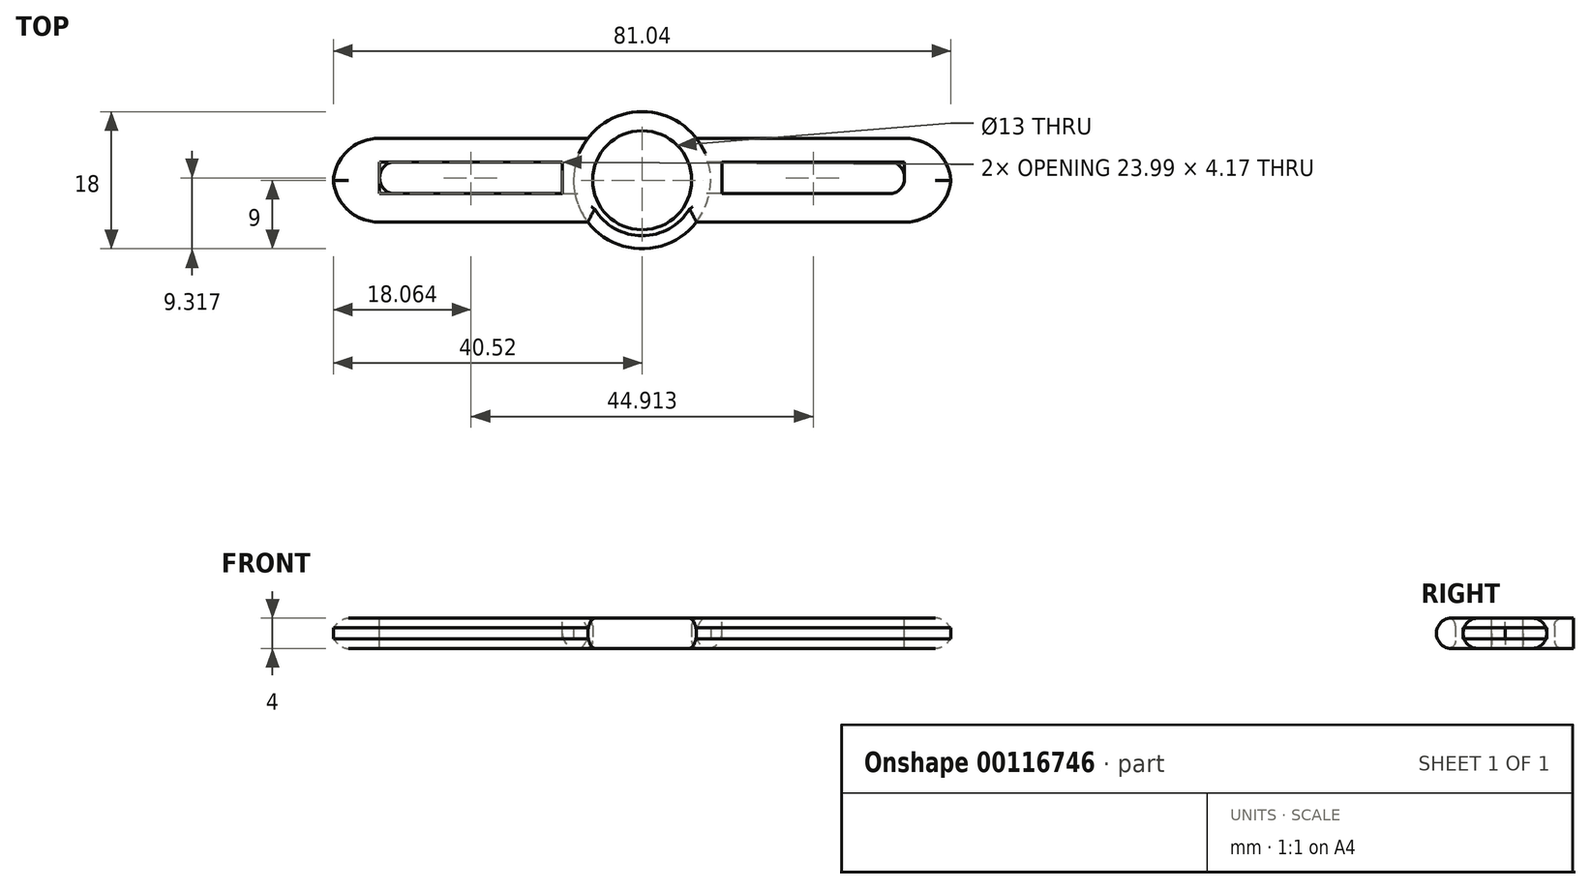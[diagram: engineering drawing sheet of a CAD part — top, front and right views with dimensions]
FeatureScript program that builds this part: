
annotation { "Feature Type Name" : "Feature", "Feature Type Description" : "" }
export const myFeature = defineFeature(function(context is Context, id is Id, definition is map)
    precondition{}
    {
        {
            var Q0;
            Q0=qCreatedBy(makeId("Top.planeOp"),FACE);
            var sketch = newSketch(context, id + "F0", { "sketchPlane" : qUnion([Q0])});
            skCircle(sketch, "E0", {"center": v(0, 0) * mm, "radius": 9 * mm});
            skCircle(sketch, "E1", {"center": v(0, 0) * mm, "radius": 6.5 * mm});
            skLineSegment(sketch, "E2.bottom", {"start": v(-40.54, -5.5) * mm, "end": v(40.54, -5.5) * mm});
            skLineSegment(sketch, "E2.top", {"start": v(-40.54, 5.5) * mm, "end": v(40.54, 5.5) * mm});
            skLineSegment(sketch, "E2.left", {"start": v(-40.54, -5.5) * mm, "end": v(-40.54, 5.5) * mm});
            skLineSegment(sketch, "E2.right", {"start": v(40.54, -5.5) * mm, "end": v(40.54, 5.5) * mm});
            skSolve(sketch);
        }
        {
            var Q0;
            {var subQ5=sQuery(id+"F0.wireOp",EDGE,"E2.left");Q0=makeQuery(id+"F0.imprint","IMPRINT",FACE,{"disambiguationData":[TD([[makeQuery(id+"F0.imprint","IMPRINT",EDGE,{"derivedFrom":subQ5}),-1.0]])]});}
            var Q1;
            {var subQ5=sQuery(id+"F0.wireOp",EDGE,"E2.right");Q1=makeQuery(id+"F0.imprint","IMPRINT",FACE,{"disambiguationData":[TD([[makeQuery(id+"F0.imprint","IMPRINT",EDGE,{"derivedFrom":subQ5}),1.0]])]});}
            extrude(context, id + "F1", {"entities" : qUnion([Q0, Q1]), "endBound" : BoundingType.SYMMETRIC, "depth" : 1.5 * mm});
        }
        {
            var Q0;
            Q0 = qSketchRegion(id + "F0", true);
            extrude(context, id + "F2", {"entities" : qUnion([Q0]), "endBound" : BoundingType.SYMMETRIC, "depth" : 4 * mm});
        }
        {
            var Q0;
            Q0=makeQuery(id+"F2.opExtrude","SWEPT_EDGE",EDGE,{"disambiguationData":[OSD([sQuery(id+"F0.wireOp",EDGE,"E2.top"),sQuery(id+"F0.wireOp",EDGE,"E2.left")])]});
            var Q1;
            Q1=makeQuery(id+"F2.opExtrude","SWEPT_EDGE",EDGE,{"disambiguationData":[OSD([sQuery(id+"F0.wireOp",EDGE,"E2.bottom"),sQuery(id+"F0.wireOp",EDGE,"E2.left")])]});
            var Q2;
            Q2=makeQuery(id+"F2.opExtrude","SWEPT_EDGE",EDGE,{"disambiguationData":[OSD([sQuery(id+"F0.wireOp",EDGE,"E2.top"),sQuery(id+"F0.wireOp",EDGE,"E2.right")])]});
            var Q3;
            Q3=makeQuery(id+"F2.opExtrude","SWEPT_EDGE",EDGE,{"disambiguationData":[OSD([sQuery(id+"F0.wireOp",EDGE,"E2.bottom"),sQuery(id+"F0.wireOp",EDGE,"E2.right")])]});
            fillet(context, id + "F3", {"entities" : qUnion([Q0, Q1, Q2, Q3]), "radius" : 6 * mm, "tangentPropagation" : true, "allowEdgeOverflow" : false});
        }
        {
            var Q0;
            Q0=makeQuery(id+"F1.opExtrude","SWEPT_EDGE",EDGE,{"disambiguationData":[OSD([sQuery(id+"F0.wireOp",EDGE,"E2.top"),sQuery(id+"F0.wireOp",EDGE,"E2.right")])]});
            var Q1;
            Q1=makeQuery(id+"F1.opExtrude","SWEPT_EDGE",EDGE,{"disambiguationData":[OSD([sQuery(id+"F0.wireOp",EDGE,"E2.bottom"),sQuery(id+"F0.wireOp",EDGE,"E2.right")])]});
            var Q2;
            Q2=makeQuery(id+"F1.opExtrude","SWEPT_EDGE",EDGE,{"disambiguationData":[OSD([sQuery(id+"F0.wireOp",EDGE,"E2.top"),sQuery(id+"F0.wireOp",EDGE,"E2.left")])]});
            var Q3;
            Q3=makeQuery(id+"F1.opExtrude","SWEPT_EDGE",EDGE,{"disambiguationData":[OSD([sQuery(id+"F0.wireOp",EDGE,"E2.bottom"),sQuery(id+"F0.wireOp",EDGE,"E2.left")])]});
            fillet(context, id + "F4", {"entities" : qUnion([Q0, Q1, Q2, Q3]), "radius" : 6 * mm, "tangentPropagation" : true, "allowEdgeOverflow" : false});
        }
        {
            var Q0;
            {var subQ0=sQuery(id+"F0.wireOp",EDGE,"E2.left");var subQ1=sQuery(id+"F0.wireOp",EDGE,"E2.bottom");Q0=makeQuery(id+"F3.opFillet","BLEND_EDGE",EDGE,{"blendedFrom":[makeQuery(id+"F2.opExtrude","SWEPT_EDGE",EDGE,{"disambiguationData":[OSD([subQ1,subQ0])]}),makeQuery(id+"F2.opExtrude","CAP_FACE",FACE,{"disambiguationData":[OSD([sQuery(id+"F0.wireOp",EDGE,"E0"),sQuery(id+"F0.wireOp",EDGE,"E1"),subQ1,sQuery(id+"F0.wireOp",EDGE,"E2.top"),subQ0,sQuery(id+"F0.wireOp",EDGE,"E2.right")])],"isStart":false})],"blendedInto":[makeQuery(id+"F2.opExtrude","CAP_FACE",FACE,{"disambiguationData":[OSD([sQuery(id+"F0.wireOp",EDGE,"E0"),sQuery(id+"F0.wireOp",EDGE,"E1"),subQ1,sQuery(id+"F0.wireOp",EDGE,"E2.top"),subQ0,sQuery(id+"F0.wireOp",EDGE,"E2.right")])],"isStart":false})]});}
            var Q1;
            {var subQ0=sQuery(id+"F0.wireOp",EDGE,"E2.left");var subQ1=sQuery(id+"F0.wireOp",EDGE,"E2.top");Q1=makeQuery(id+"F3.opFillet","BLEND_EDGE",EDGE,{"blendedFrom":[makeQuery(id+"F2.opExtrude","SWEPT_EDGE",EDGE,{"disambiguationData":[OSD([subQ1,subQ0])]}),makeQuery(id+"F2.opExtrude","CAP_FACE",FACE,{"disambiguationData":[OSD([sQuery(id+"F0.wireOp",EDGE,"E0"),sQuery(id+"F0.wireOp",EDGE,"E1"),sQuery(id+"F0.wireOp",EDGE,"E2.bottom"),subQ1,subQ0,sQuery(id+"F0.wireOp",EDGE,"E2.right")])],"isStart":false})],"blendedInto":[makeQuery(id+"F2.opExtrude","CAP_FACE",FACE,{"disambiguationData":[OSD([sQuery(id+"F0.wireOp",EDGE,"E0"),sQuery(id+"F0.wireOp",EDGE,"E1"),sQuery(id+"F0.wireOp",EDGE,"E2.bottom"),subQ1,subQ0,sQuery(id+"F0.wireOp",EDGE,"E2.right")])],"isStart":false})]});}
            var Q2;
            {var subQ0=sQuery(id+"F0.wireOp",EDGE,"E2.top");Q2=makeQuery(id+"F2.opExtrude","CAP_EDGE",EDGE,{"disambiguationData":[OSD([subQ0]),TDD([makeQuery(id+"F0.imprint","IMPRINT",EDGE,{"disambiguationData":[TD([[makeQuery(id+"F0.imprint","INTERSECT",VERTEX,{"derivedFrom":[subQ0,sQuery(id+"F0.wireOp",EDGE,"E2.left")]}),-1.0]])],"derivedFrom":subQ0})])],"isStart":false});}
            var Q3;
            {var subQ0=sQuery(id+"F0.wireOp",EDGE,"E2.bottom");Q3=makeQuery(id+"F2.opExtrude","CAP_EDGE",EDGE,{"disambiguationData":[OSD([subQ0]),TDD([makeQuery(id+"F0.imprint","IMPRINT",EDGE,{"disambiguationData":[TD([[makeQuery(id+"F0.imprint","INTERSECT",VERTEX,{"derivedFrom":[subQ0,sQuery(id+"F0.wireOp",EDGE,"E2.left")]}),-1.0]])],"derivedFrom":subQ0})])],"isStart":false});}
            var Q4;
            {var subQ0=sQuery(id+"F0.wireOp",EDGE,"E2.bottom");Q4=makeQuery(id+"F2.opExtrude","CAP_EDGE",EDGE,{"disambiguationData":[OSD([subQ0]),TDD([makeQuery(id+"F0.imprint","IMPRINT",EDGE,{"disambiguationData":[TD([[makeQuery(id+"F0.imprint","INTERSECT",VERTEX,{"derivedFrom":[subQ0,sQuery(id+"F0.wireOp",EDGE,"E2.right")]}),1.0]])],"derivedFrom":subQ0})])],"isStart":false});}
            var Q5;
            {var subQ0=sQuery(id+"F0.wireOp",EDGE,"E2.right");var subQ1=sQuery(id+"F0.wireOp",EDGE,"E2.bottom");Q5=makeQuery(id+"F3.opFillet","BLEND_EDGE",EDGE,{"blendedFrom":[makeQuery(id+"F2.opExtrude","SWEPT_EDGE",EDGE,{"disambiguationData":[OSD([subQ1,subQ0])]}),makeQuery(id+"F2.opExtrude","CAP_FACE",FACE,{"disambiguationData":[OSD([sQuery(id+"F0.wireOp",EDGE,"E0"),sQuery(id+"F0.wireOp",EDGE,"E1"),subQ1,sQuery(id+"F0.wireOp",EDGE,"E2.top"),sQuery(id+"F0.wireOp",EDGE,"E2.left"),subQ0])],"isStart":false})],"blendedInto":[makeQuery(id+"F2.opExtrude","CAP_FACE",FACE,{"disambiguationData":[OSD([sQuery(id+"F0.wireOp",EDGE,"E0"),sQuery(id+"F0.wireOp",EDGE,"E1"),subQ1,sQuery(id+"F0.wireOp",EDGE,"E2.top"),sQuery(id+"F0.wireOp",EDGE,"E2.left"),subQ0])],"isStart":false})]});}
            var Q6;
            {var subQ0=sQuery(id+"F0.wireOp",EDGE,"E2.right");var subQ1=sQuery(id+"F0.wireOp",EDGE,"E2.top");Q6=makeQuery(id+"F3.opFillet","BLEND_EDGE",EDGE,{"blendedFrom":[makeQuery(id+"F2.opExtrude","SWEPT_EDGE",EDGE,{"disambiguationData":[OSD([subQ1,subQ0])]}),makeQuery(id+"F2.opExtrude","CAP_FACE",FACE,{"disambiguationData":[OSD([sQuery(id+"F0.wireOp",EDGE,"E0"),sQuery(id+"F0.wireOp",EDGE,"E1"),sQuery(id+"F0.wireOp",EDGE,"E2.bottom"),subQ1,sQuery(id+"F0.wireOp",EDGE,"E2.left"),subQ0])],"isStart":false})],"blendedInto":[makeQuery(id+"F2.opExtrude","CAP_FACE",FACE,{"disambiguationData":[OSD([sQuery(id+"F0.wireOp",EDGE,"E0"),sQuery(id+"F0.wireOp",EDGE,"E1"),sQuery(id+"F0.wireOp",EDGE,"E2.bottom"),subQ1,sQuery(id+"F0.wireOp",EDGE,"E2.left"),subQ0])],"isStart":false})]});}
            var Q7;
            {var subQ0=sQuery(id+"F0.wireOp",EDGE,"E2.top");Q7=makeQuery(id+"F2.opExtrude","CAP_EDGE",EDGE,{"disambiguationData":[OSD([subQ0]),TDD([makeQuery(id+"F0.imprint","IMPRINT",EDGE,{"disambiguationData":[TD([[makeQuery(id+"F0.imprint","INTERSECT",VERTEX,{"derivedFrom":[subQ0,sQuery(id+"F0.wireOp",EDGE,"E2.right")]}),1.0]])],"derivedFrom":subQ0})])],"isStart":false});}
            var Q8;
            {var subQ0=sQuery(id+"F0.wireOp",EDGE,"E2.top");var subQ1=sQuery(id+"F0.wireOp",EDGE,"E0");Q8=makeQuery(id+"F2.opExtrude","CAP_EDGE",EDGE,{"disambiguationData":[OSD([subQ1]),TDD([makeQuery(id+"F0.imprint","IMPRINT",EDGE,{"disambiguationData":[TD([[makeQuery(id+"F0.imprint","INTERSECT",VERTEX,{"disambiguationData":[OD(0.0)],"derivedFrom":[subQ1,subQ0]}),1.0]])],"derivedFrom":subQ1})])],"isStart":false});}
            var Q9;
            {var subQ0=sQuery(id+"F0.wireOp",EDGE,"E2.bottom");var subQ1=sQuery(id+"F0.wireOp",EDGE,"E0");Q9=makeQuery(id+"F2.opExtrude","CAP_EDGE",EDGE,{"disambiguationData":[OSD([subQ1]),TDD([makeQuery(id+"F0.imprint","IMPRINT",EDGE,{"disambiguationData":[TD([[makeQuery(id+"F0.imprint","INTERSECT",VERTEX,{"disambiguationData":[OD(0.0)],"derivedFrom":[subQ1,subQ0]}),-1.0]])],"derivedFrom":subQ1})])],"isStart":false});}
            var Q10;
            {var subQ0=sQuery(id+"F0.wireOp",EDGE,"E2.bottom");var subQ1=sQuery(id+"F0.wireOp",EDGE,"E0");Q10=makeQuery(id+"F2.opExtrude","CAP_EDGE",EDGE,{"disambiguationData":[OSD([subQ1]),TDD([makeQuery(id+"F0.imprint","IMPRINT",EDGE,{"disambiguationData":[TD([[makeQuery(id+"F0.imprint","INTERSECT",VERTEX,{"disambiguationData":[OD(0.0)],"derivedFrom":[subQ1,subQ0]}),-1.0]])],"derivedFrom":subQ1})])],"isStart":true});}
            var Q11;
            {var subQ0=sQuery(id+"F0.wireOp",EDGE,"E2.top");var subQ1=sQuery(id+"F0.wireOp",EDGE,"E0");Q11=makeQuery(id+"F2.opExtrude","CAP_EDGE",EDGE,{"disambiguationData":[OSD([subQ1]),TDD([makeQuery(id+"F0.imprint","IMPRINT",EDGE,{"disambiguationData":[TD([[makeQuery(id+"F0.imprint","INTERSECT",VERTEX,{"disambiguationData":[OD(0.0)],"derivedFrom":[subQ1,subQ0]}),1.0]])],"derivedFrom":subQ1})])],"isStart":true});}
            var Q12;
            {var subQ0=sQuery(id+"F0.wireOp",EDGE,"E2.bottom");Q12=makeQuery(id+"F2.opExtrude","CAP_EDGE",EDGE,{"disambiguationData":[OSD([subQ0]),TDD([makeQuery(id+"F0.imprint","IMPRINT",EDGE,{"disambiguationData":[TD([[makeQuery(id+"F0.imprint","INTERSECT",VERTEX,{"derivedFrom":[subQ0,sQuery(id+"F0.wireOp",EDGE,"E2.left")]}),-1.0]])],"derivedFrom":subQ0})])],"isStart":true});}
            var Q13;
            {var subQ0=sQuery(id+"F0.wireOp",EDGE,"E2.top");Q13=makeQuery(id+"F2.opExtrude","CAP_EDGE",EDGE,{"disambiguationData":[OSD([subQ0]),TDD([makeQuery(id+"F0.imprint","IMPRINT",EDGE,{"disambiguationData":[TD([[makeQuery(id+"F0.imprint","INTERSECT",VERTEX,{"derivedFrom":[subQ0,sQuery(id+"F0.wireOp",EDGE,"E2.left")]}),-1.0]])],"derivedFrom":subQ0})])],"isStart":true});}
            var Q14;
            {var subQ0=sQuery(id+"F0.wireOp",EDGE,"E2.top");Q14=makeQuery(id+"F2.opExtrude","CAP_EDGE",EDGE,{"disambiguationData":[OSD([subQ0]),TDD([makeQuery(id+"F0.imprint","IMPRINT",EDGE,{"disambiguationData":[TD([[makeQuery(id+"F0.imprint","INTERSECT",VERTEX,{"derivedFrom":[subQ0,sQuery(id+"F0.wireOp",EDGE,"E2.right")]}),1.0]])],"derivedFrom":subQ0})])],"isStart":true});}
            var Q15;
            {var subQ0=sQuery(id+"F0.wireOp",EDGE,"E2.bottom");Q15=makeQuery(id+"F2.opExtrude","CAP_EDGE",EDGE,{"disambiguationData":[OSD([subQ0]),TDD([makeQuery(id+"F0.imprint","IMPRINT",EDGE,{"disambiguationData":[TD([[makeQuery(id+"F0.imprint","INTERSECT",VERTEX,{"derivedFrom":[subQ0,sQuery(id+"F0.wireOp",EDGE,"E2.right")]}),1.0]])],"derivedFrom":subQ0})])],"isStart":true});}
            var Q16;
            {var subQ0=sQuery(id+"F0.wireOp",EDGE,"E2.right");var subQ1=sQuery(id+"F0.wireOp",EDGE,"E2.bottom");Q16=makeQuery(id+"F3.opFillet","BLEND_EDGE",EDGE,{"blendedFrom":[makeQuery(id+"F2.opExtrude","SWEPT_EDGE",EDGE,{"disambiguationData":[OSD([subQ1,subQ0])]}),makeQuery(id+"F2.opExtrude","CAP_FACE",FACE,{"disambiguationData":[OSD([sQuery(id+"F0.wireOp",EDGE,"E0"),sQuery(id+"F0.wireOp",EDGE,"E1"),subQ1,sQuery(id+"F0.wireOp",EDGE,"E2.top"),sQuery(id+"F0.wireOp",EDGE,"E2.left"),subQ0])],"isStart":true})],"blendedInto":[makeQuery(id+"F2.opExtrude","CAP_FACE",FACE,{"disambiguationData":[OSD([sQuery(id+"F0.wireOp",EDGE,"E0"),sQuery(id+"F0.wireOp",EDGE,"E1"),subQ1,sQuery(id+"F0.wireOp",EDGE,"E2.top"),sQuery(id+"F0.wireOp",EDGE,"E2.left"),subQ0])],"isStart":true})]});}
            var Q17;
            {var subQ0=sQuery(id+"F0.wireOp",EDGE,"E2.right");var subQ1=sQuery(id+"F0.wireOp",EDGE,"E2.top");Q17=makeQuery(id+"F3.opFillet","BLEND_EDGE",EDGE,{"blendedFrom":[makeQuery(id+"F2.opExtrude","SWEPT_EDGE",EDGE,{"disambiguationData":[OSD([subQ1,subQ0])]}),makeQuery(id+"F2.opExtrude","CAP_FACE",FACE,{"disambiguationData":[OSD([sQuery(id+"F0.wireOp",EDGE,"E0"),sQuery(id+"F0.wireOp",EDGE,"E1"),sQuery(id+"F0.wireOp",EDGE,"E2.bottom"),subQ1,sQuery(id+"F0.wireOp",EDGE,"E2.left"),subQ0])],"isStart":true})],"blendedInto":[makeQuery(id+"F2.opExtrude","CAP_FACE",FACE,{"disambiguationData":[OSD([sQuery(id+"F0.wireOp",EDGE,"E0"),sQuery(id+"F0.wireOp",EDGE,"E1"),sQuery(id+"F0.wireOp",EDGE,"E2.bottom"),subQ1,sQuery(id+"F0.wireOp",EDGE,"E2.left"),subQ0])],"isStart":true})]});}
            var Q18;
            {var subQ0=sQuery(id+"F0.wireOp",EDGE,"E2.left");var subQ1=sQuery(id+"F0.wireOp",EDGE,"E2.top");Q18=makeQuery(id+"F3.opFillet","BLEND_EDGE",EDGE,{"blendedFrom":[makeQuery(id+"F2.opExtrude","SWEPT_EDGE",EDGE,{"disambiguationData":[OSD([subQ1,subQ0])]}),makeQuery(id+"F2.opExtrude","CAP_FACE",FACE,{"disambiguationData":[OSD([sQuery(id+"F0.wireOp",EDGE,"E0"),sQuery(id+"F0.wireOp",EDGE,"E1"),sQuery(id+"F0.wireOp",EDGE,"E2.bottom"),subQ1,subQ0,sQuery(id+"F0.wireOp",EDGE,"E2.right")])],"isStart":true})],"blendedInto":[makeQuery(id+"F2.opExtrude","CAP_FACE",FACE,{"disambiguationData":[OSD([sQuery(id+"F0.wireOp",EDGE,"E0"),sQuery(id+"F0.wireOp",EDGE,"E1"),sQuery(id+"F0.wireOp",EDGE,"E2.bottom"),subQ1,subQ0,sQuery(id+"F0.wireOp",EDGE,"E2.right")])],"isStart":true})]});}
            var Q19;
            {var subQ0=sQuery(id+"F0.wireOp",EDGE,"E2.left");var subQ1=sQuery(id+"F0.wireOp",EDGE,"E2.bottom");Q19=makeQuery(id+"F3.opFillet","BLEND_EDGE",EDGE,{"blendedFrom":[makeQuery(id+"F2.opExtrude","SWEPT_EDGE",EDGE,{"disambiguationData":[OSD([subQ1,subQ0])]}),makeQuery(id+"F2.opExtrude","CAP_FACE",FACE,{"disambiguationData":[OSD([sQuery(id+"F0.wireOp",EDGE,"E0"),sQuery(id+"F0.wireOp",EDGE,"E1"),subQ1,sQuery(id+"F0.wireOp",EDGE,"E2.top"),subQ0,sQuery(id+"F0.wireOp",EDGE,"E2.right")])],"isStart":true})],"blendedInto":[makeQuery(id+"F2.opExtrude","CAP_FACE",FACE,{"disambiguationData":[OSD([sQuery(id+"F0.wireOp",EDGE,"E0"),sQuery(id+"F0.wireOp",EDGE,"E1"),subQ1,sQuery(id+"F0.wireOp",EDGE,"E2.top"),subQ0,sQuery(id+"F0.wireOp",EDGE,"E2.right")])],"isStart":true})]});}
            fillet(context, id + "F5", {"entities" : qUnion([Q0, Q1, Q2, Q3, Q4, Q5, Q6, Q7, Q8, Q9, Q10, Q11, Q12, Q13, Q14, Q15, Q16, Q17, Q18, Q19]), "radius" : 2 * mm, "tangentPropagation" : true, "allowEdgeOverflow" : false});
        }
        {
            var Q0;
            Q0=makeQuery(id+"F2.opExtrude","CAP_EDGE",EDGE,{"disambiguationData":[OSD([sQuery(id+"F0.wireOp",EDGE,"E1")])],"isStart":false});
            var Q1;
            Q1=makeQuery(id+"F2.opExtrude","CAP_EDGE",EDGE,{"disambiguationData":[OSD([sQuery(id+"F0.wireOp",EDGE,"E1")])],"isStart":true});
            fillet(context, id + "F6", {"entities" : qUnion([Q0, Q1]), "radius" : 1 * mm, "tangentPropagation" : true, "allowEdgeOverflow" : false});
        }
        {
            var Q0;
            Q0=makeQuery(id+"F6.opFillet","SPLIT",FACE,{"disambiguationData":[OD(0.0)],"derivedFrom":makeQuery(id+"F2.opExtrude","CAP_FACE",FACE,{"disambiguationData":[OSD([sQuery(id+"F0.wireOp",EDGE,"E0"),sQuery(id+"F0.wireOp",EDGE,"E1"),sQuery(id+"F0.wireOp",EDGE,"E2.bottom"),sQuery(id+"F0.wireOp",EDGE,"E2.top"),sQuery(id+"F0.wireOp",EDGE,"E2.left"),sQuery(id+"F0.wireOp",EDGE,"E2.right")])],"isStart":false})});
            var sketch = newSketch(context, id + "F7", { "sketchPlane" : qUnion([Q0])});
            skLineSegment(sketch, "E3.bottom", {"start": v(-34.45, 2.4) * mm, "end": v(-10.46, 2.4) * mm});
            skLineSegment(sketch, "E3.top", {"start": v(-34.45, -1.77) * mm, "end": v(-10.46, -1.77) * mm});
            skLineSegment(sketch, "E3.left", {"start": v(-34.45, 2.4) * mm, "end": v(-34.45, -1.77) * mm});
            skLineSegment(sketch, "E3.right", {"start": v(-10.46, 2.4) * mm, "end": v(-10.46, -1.77) * mm});
            skLineSegment(sketch, "E4.MirrorCS", {"start": v(34.45, 2.4) * mm, "end": v(34.45, -1.77) * mm});
            skLineSegment(sketch, "E5.MirrorCS", {"start": v(34.45, 2.4) * mm, "end": v(10.46, 2.4) * mm});
            skLineSegment(sketch, "E6.MirrorCS", {"start": v(34.45, -1.77) * mm, "end": v(10.46, -1.77) * mm});
            skLineSegment(sketch, "E7.MirrorCS", {"start": v(10.46, 2.4) * mm, "end": v(10.46, -1.77) * mm});
            skSolve(sketch);
        }
        {
            var Q0;
            Q0 = qSketchRegion(id + "F7", true);
            extrude(context, id + "F8", {"entities" : qUnion([Q0]), "operationType" : NewBodyOperationType.REMOVE, "endBound" : BoundingType.THROUGH_ALL, "oppositeDirection" : true, "depth" : 25 * mm});
        }
        {
            var Q0;
            {var subQ0=sQuery(id+"F0.wireOp",EDGE,"E2.right");var subQ1=sQuery(id+"F0.wireOp",EDGE,"E2.left");var subQ2=sQuery(id+"F0.wireOp",EDGE,"E2.top");var subQ3=sQuery(id+"F0.wireOp",EDGE,"E2.bottom");var subQ4=sQuery(id+"F0.wireOp",EDGE,"E1");var subQ5=sQuery(id+"F0.wireOp",EDGE,"E0");var subQ6=sQuery(id+"F7.wireOp",EDGE,"E3.bottom");var subQ7=sQuery(id+"F7.wireOp",EDGE,"E3.left");Q0=makeQuery(id+"F8.boolean.opBoolean","COPY",EDGE,{"disambiguationData":[TD([makeQuery(id+"F2.opExtrude","CAP_FACE",FACE,{"disambiguationData":[OSD([subQ5,subQ4,subQ3,subQ2,subQ1,subQ0])],"isStart":true})])],"derivedFrom":makeQuery(id+"F8.opExtrude","SWEPT_EDGE",EDGE,{"disambiguationData":[OSD([subQ6,subQ7])]})});}
            var Q1;
            {var subQ0=sQuery(id+"F0.wireOp",EDGE,"E2.right");var subQ1=sQuery(id+"F0.wireOp",EDGE,"E2.left");var subQ2=sQuery(id+"F0.wireOp",EDGE,"E2.top");var subQ3=sQuery(id+"F0.wireOp",EDGE,"E2.bottom");var subQ4=sQuery(id+"F0.wireOp",EDGE,"E1");var subQ5=sQuery(id+"F0.wireOp",EDGE,"E0");var subQ6=sQuery(id+"F7.wireOp",EDGE,"E3.top");var subQ7=sQuery(id+"F7.wireOp",EDGE,"E3.left");Q1=makeQuery(id+"F8.boolean.opBoolean","COPY",EDGE,{"disambiguationData":[TD([makeQuery(id+"F2.opExtrude","CAP_FACE",FACE,{"disambiguationData":[OSD([subQ5,subQ4,subQ3,subQ2,subQ1,subQ0])],"isStart":true})])],"derivedFrom":makeQuery(id+"F8.opExtrude","SWEPT_EDGE",EDGE,{"disambiguationData":[OSD([subQ6,subQ7])]})});}
            var Q2;
            {var subQ0=sQuery(id+"F0.wireOp",EDGE,"E2.right");var subQ1=sQuery(id+"F0.wireOp",EDGE,"E2.top");var subQ2=sQuery(id+"F0.wireOp",EDGE,"E2.bottom");var subQ3=sQuery(id+"F0.wireOp",EDGE,"E0");var subQ4=sQuery(id+"F7.wireOp",EDGE,"E4.MirrorCS");var subQ5=sQuery(id+"F7.wireOp",EDGE,"E6.MirrorCS");Q2=makeQuery(id+"F8.boolean.opBoolean","COPY",EDGE,{"disambiguationData":[TD([makeQuery(id+"F1.opExtrude","CAP_FACE",FACE,{"disambiguationData":[OSD([subQ3,subQ2,subQ1,subQ0])],"isStart":true})])],"derivedFrom":makeQuery(id+"F8.opExtrude","SWEPT_EDGE",EDGE,{"disambiguationData":[OSD([subQ4,subQ5])]})});}
            var Q3;
            {var subQ0=sQuery(id+"F0.wireOp",EDGE,"E2.right");var subQ1=sQuery(id+"F0.wireOp",EDGE,"E2.left");var subQ2=sQuery(id+"F0.wireOp",EDGE,"E2.top");var subQ3=sQuery(id+"F0.wireOp",EDGE,"E2.bottom");var subQ4=sQuery(id+"F0.wireOp",EDGE,"E1");var subQ5=sQuery(id+"F0.wireOp",EDGE,"E0");var subQ6=sQuery(id+"F7.wireOp",EDGE,"E6.MirrorCS");var subQ7=sQuery(id+"F7.wireOp",EDGE,"E4.MirrorCS");Q3=makeQuery(id+"F8.boolean.opBoolean","COPY",EDGE,{"disambiguationData":[TD([makeQuery(id+"F2.opExtrude","CAP_FACE",FACE,{"disambiguationData":[OSD([subQ5,subQ4,subQ3,subQ2,subQ1,subQ0])],"isStart":true})])],"derivedFrom":makeQuery(id+"F8.opExtrude","SWEPT_EDGE",EDGE,{"disambiguationData":[OSD([subQ7,subQ6])]})});}
            var Q4;
            {var subQ0=sQuery(id+"F0.wireOp",EDGE,"E2.right");var subQ1=sQuery(id+"F0.wireOp",EDGE,"E2.left");var subQ2=sQuery(id+"F0.wireOp",EDGE,"E2.top");var subQ3=sQuery(id+"F0.wireOp",EDGE,"E2.bottom");var subQ4=sQuery(id+"F0.wireOp",EDGE,"E1");var subQ5=sQuery(id+"F0.wireOp",EDGE,"E0");var subQ6=sQuery(id+"F7.wireOp",EDGE,"E4.MirrorCS");var subQ7=sQuery(id+"F7.wireOp",EDGE,"E5.MirrorCS");Q4=makeQuery(id+"F8.boolean.opBoolean","COPY",EDGE,{"disambiguationData":[TD([makeQuery(id+"F2.opExtrude","CAP_FACE",FACE,{"disambiguationData":[OSD([subQ5,subQ4,subQ3,subQ2,subQ1,subQ0])],"isStart":true})])],"derivedFrom":makeQuery(id+"F8.opExtrude","SWEPT_EDGE",EDGE,{"disambiguationData":[OSD([subQ6,subQ7])]})});}
            fillet(context, id + "F9", {"entities" : qUnion([Q0, Q1, Q2, Q3, Q4]), "radius" : 2 * mm, "tangentPropagation" : true, "allowEdgeOverflow" : false});
        }
        {
            var Q0;
            Q0=makeQuery(id+"F8.boolean.opBoolean","COPY",EDGE,{"derivedFrom":makeQuery(id+"F8.opExtrude","CAP_EDGE",EDGE,{"disambiguationData":[OSD([sQuery(id+"F7.wireOp",EDGE,"E3.right")])],"isStart":true})});
            var Q1;
            Q1=makeQuery(id+"F8.boolean.opBoolean","INTERSECT",EDGE,{"derivedFrom":[makeQuery(id+"F6.opFillet","SPLIT",FACE,{"disambiguationData":[OD(1.0)],"derivedFrom":makeQuery(id+"F2.opExtrude","CAP_FACE",FACE,{"disambiguationData":[OSD([sQuery(id+"F0.wireOp",EDGE,"E0"),sQuery(id+"F0.wireOp",EDGE,"E1"),sQuery(id+"F0.wireOp",EDGE,"E2.bottom"),sQuery(id+"F0.wireOp",EDGE,"E2.top"),sQuery(id+"F0.wireOp",EDGE,"E2.left"),sQuery(id+"F0.wireOp",EDGE,"E2.right")])],"isStart":true})}),makeQuery(id+"F8.opExtrude","SWEPT_FACE",FACE,{"disambiguationData":[OSD([sQuery(id+"F7.wireOp",EDGE,"E7.MirrorCS")])]})]});
            var Q2;
            Q2=makeQuery(id+"F8.boolean.opBoolean","INTERSECT",EDGE,{"derivedFrom":[makeQuery(id+"F6.opFillet","SPLIT",FACE,{"disambiguationData":[OD(0.0)],"derivedFrom":makeQuery(id+"F2.opExtrude","CAP_FACE",FACE,{"disambiguationData":[OSD([sQuery(id+"F0.wireOp",EDGE,"E0"),sQuery(id+"F0.wireOp",EDGE,"E1"),sQuery(id+"F0.wireOp",EDGE,"E2.bottom"),sQuery(id+"F0.wireOp",EDGE,"E2.top"),sQuery(id+"F0.wireOp",EDGE,"E2.left"),sQuery(id+"F0.wireOp",EDGE,"E2.right")])],"isStart":true})}),makeQuery(id+"F8.opExtrude","SWEPT_FACE",FACE,{"disambiguationData":[OSD([sQuery(id+"F7.wireOp",EDGE,"E3.right")])]})]});
            var Q3;
            Q3=makeQuery(id+"F8.boolean.opBoolean","COPY",EDGE,{"derivedFrom":makeQuery(id+"F8.opExtrude","CAP_EDGE",EDGE,{"disambiguationData":[OSD([sQuery(id+"F7.wireOp",EDGE,"E7.MirrorCS")])],"isStart":true})});
            fillet(context, id + "F10", {"entities" : qUnion([Q0, Q1, Q2, Q3]), "radius" : 2 * mm, "tangentPropagation" : true, "allowEdgeOverflow" : false});
        }
    });
